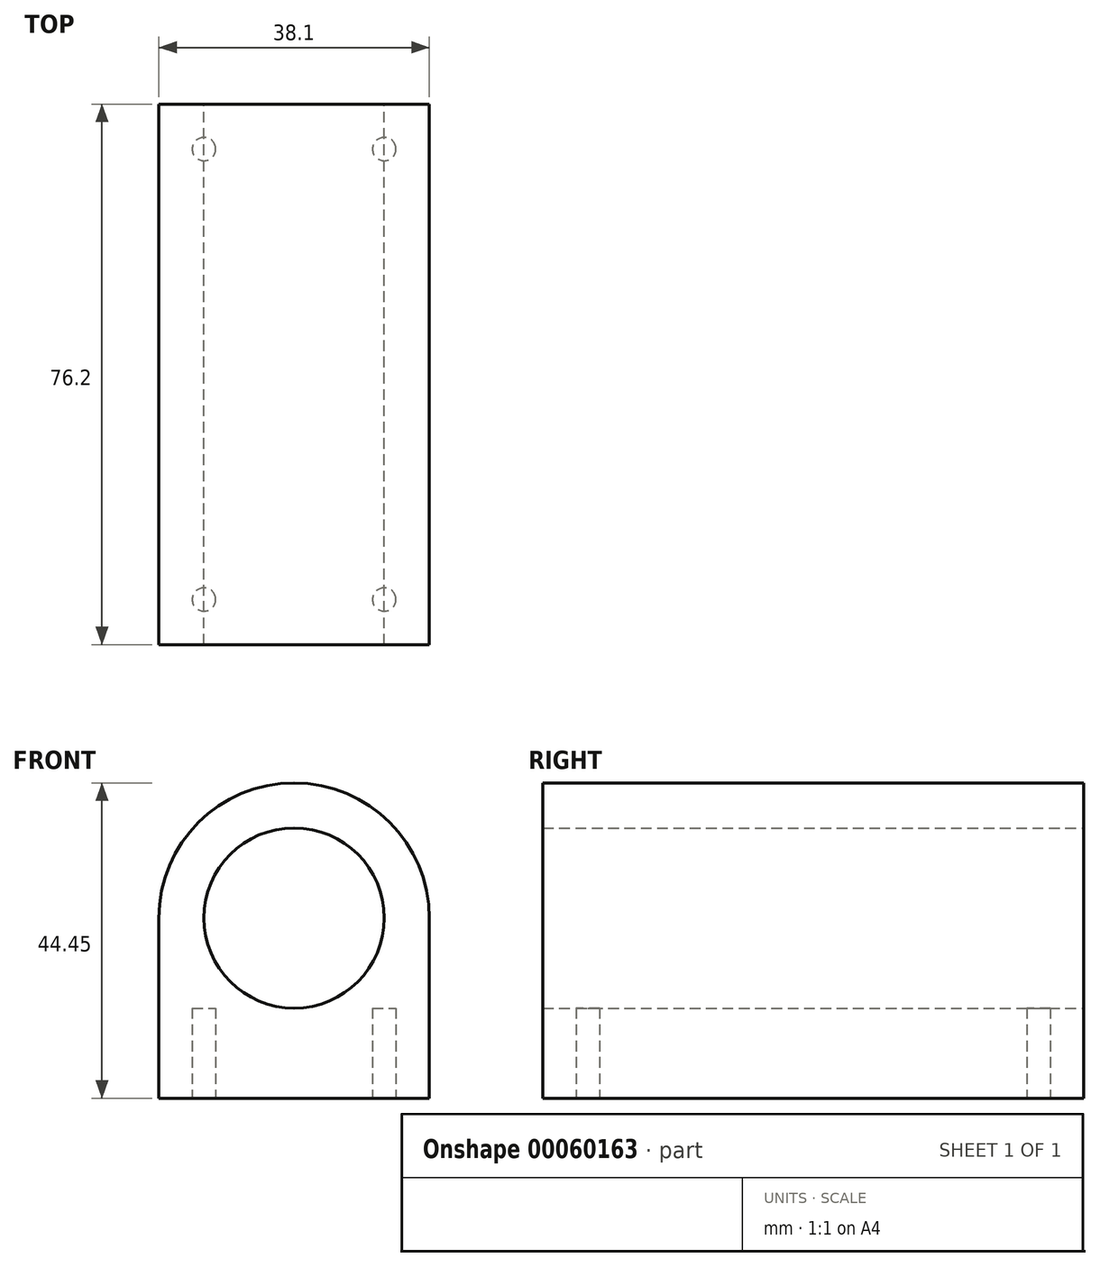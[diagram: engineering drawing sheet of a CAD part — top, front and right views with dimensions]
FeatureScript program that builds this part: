
annotation { "Feature Type Name" : "Feature", "Feature Type Description" : "" }
export const myFeature = defineFeature(function(context is Context, id is Id, definition is map)
    precondition{}
    {
        {
            var Q0;
            Q0=qCreatedBy(makeId("Front.planeOp"),FACE);
            var sketch = newSketch(context, id + "F0", { "sketchPlane" : qUnion([Q0])});
            skArc(sketch, "E0", {"start": v(19.05, 0) * mm, "mid": v(0, 19.05) * mm, "end": v(-19.05, 0) * mm});
            skCircle(sketch, "E1", {"center": v(0, 0) * mm, "radius": 12.7 * mm});
            skLineSegment(sketch, "E2", {"start": v(-19.05, 0) * mm, "end": v(-19.05, -25.4) * mm});
            skLineSegment(sketch, "E3", {"start": v(-19.05, -25.4) * mm, "end": v(19.05, -25.4) * mm});
            skLineSegment(sketch, "E4", {"start": v(19.05, -25.4) * mm, "end": v(19.05, 0) * mm});
            skSolve(sketch);
        }
        {
            var Q0;
            Q0=makeQuery(id+"F0.imprint","IMPRINT",FACE,{"disambiguationData":[TD([[makeQuery(id+"F0.imprint","IMPRINT",EDGE,{"derivedFrom":sQuery(id+"F0.wireOp",EDGE,"E0")}),1.0]])]});
            extrude(context, id + "F1", {"entities" : qUnion([Q0]), "endBound" : BoundingType.SYMMETRIC, "depth" : 76.2 * mm});
        }
        {
            var Q0;
            Q0=makeQuery(id+"F1.opExtrude","SWEPT_FACE",FACE,{"disambiguationData":[OSD([sQuery(id+"F0.wireOp",EDGE,"E3")])]});
            var sketch = newSketch(context, id + "F2", { "sketchPlane" : qUnion([Q0])});
            skLineSegment(sketch, "E5.rect.bottom", {"start": v(12.7, 31.75) * mm, "end": v(-12.7, 31.75) * mm, "construction": true});
            skLineSegment(sketch, "E5.rect.top", {"start": v(12.7, -31.75) * mm, "end": v(-12.7, -31.75) * mm, "construction": true});
            skLineSegment(sketch, "E5.rect.left", {"start": v(12.7, 31.75) * mm, "end": v(12.7, -31.75) * mm, "construction": true});
            skLineSegment(sketch, "E5.rect.right", {"start": v(-12.7, 31.75) * mm, "end": v(-12.7, -31.75) * mm, "construction": true});
            skPoint(sketch, "E5.rect.middle", {"position": v(0, 0) * mm});
            skCircle(sketch, "E6", {"center": v(12.7, 31.75) * mm, "radius": 1.65 * mm});
            skCircle(sketch, "E7", {"center": v(-12.7, 31.75) * mm, "radius": 1.65 * mm});
            skCircle(sketch, "E8", {"center": v(-12.7, -31.75) * mm, "radius": 1.65 * mm});
            skCircle(sketch, "E9", {"center": v(12.7, -31.75) * mm, "radius": 1.65 * mm});
            skSolve(sketch);
        }
        {
            var Q0;
            Q0=makeQuery(id+"F2.imprint","IMPRINT",FACE,{"disambiguationData":[TD([[makeQuery(id+"F2.imprint","IMPRINT",EDGE,{"derivedFrom":sQuery(id+"F2.wireOp",EDGE,"E7")}),1.0]])]});
            var Q1;
            Q1=makeQuery(id+"F2.imprint","IMPRINT",FACE,{"disambiguationData":[TD([[makeQuery(id+"F2.imprint","IMPRINT",EDGE,{"derivedFrom":sQuery(id+"F2.wireOp",EDGE,"E6")}),1.0]])]});
            var Q2;
            Q2=makeQuery(id+"F2.imprint","IMPRINT",FACE,{"disambiguationData":[TD([[makeQuery(id+"F2.imprint","IMPRINT",EDGE,{"derivedFrom":sQuery(id+"F2.wireOp",EDGE,"E9")}),1.0]])]});
            var Q3;
            Q3=makeQuery(id+"F2.imprint","IMPRINT",FACE,{"disambiguationData":[TD([[makeQuery(id+"F2.imprint","IMPRINT",EDGE,{"derivedFrom":sQuery(id+"F2.wireOp",EDGE,"E8")}),1.0]])]});
            extrude(context, id + "F3", {"entities" : qUnion([Q0, Q1, Q2, Q3]), "operationType" : NewBodyOperationType.REMOVE, "oppositeDirection" : true, "depth" : 12.7 * mm});
        }
    });
